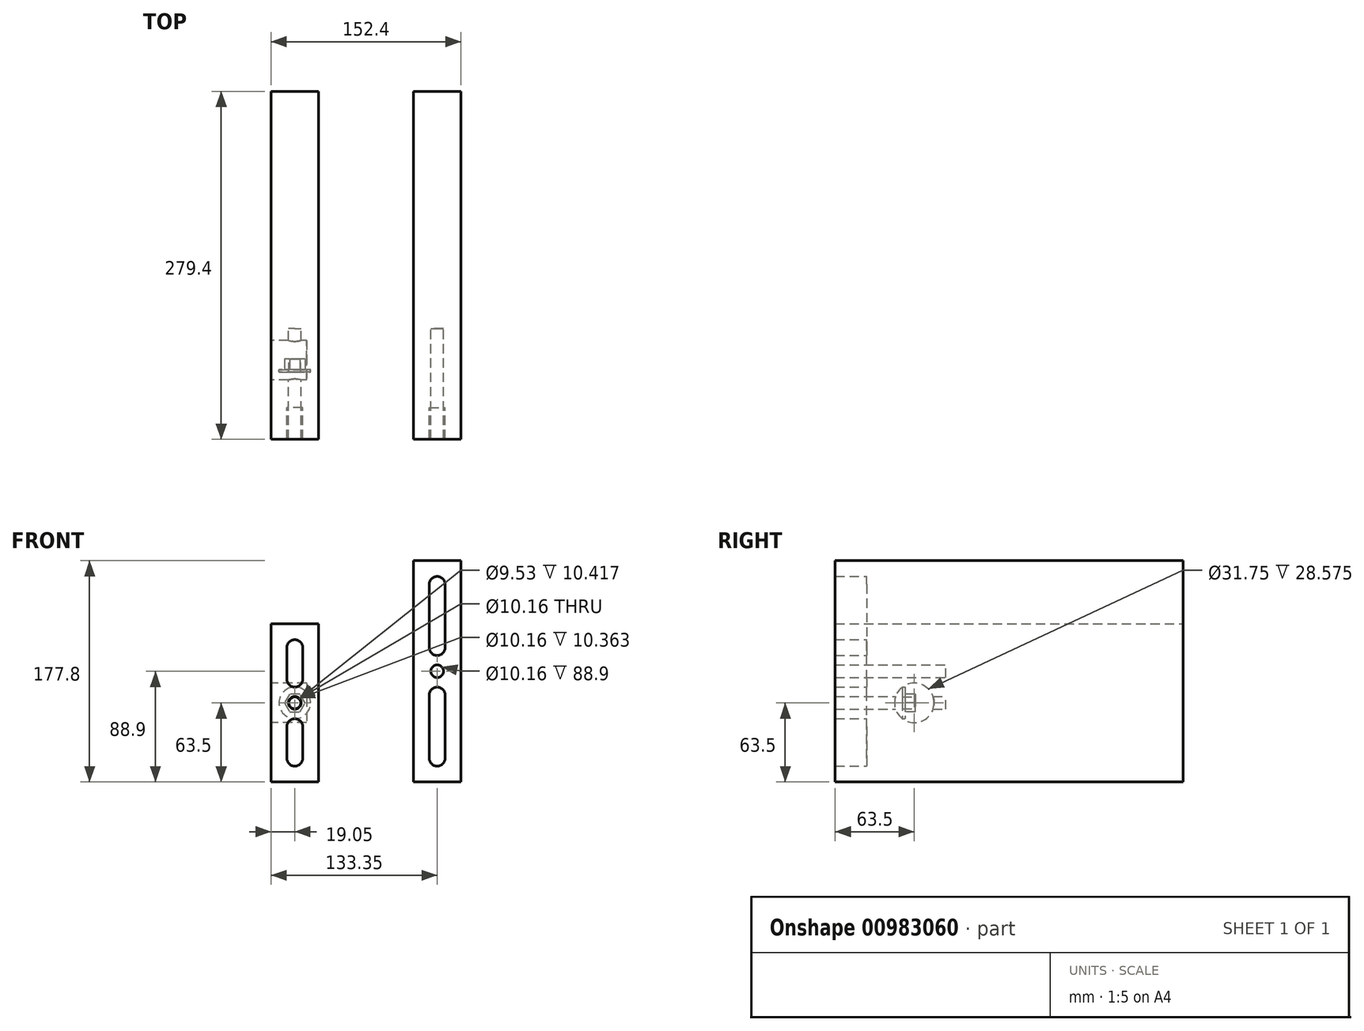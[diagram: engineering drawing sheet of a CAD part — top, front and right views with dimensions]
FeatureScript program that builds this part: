
annotation { "Feature Type Name" : "Feature", "Feature Type Description" : "" }
export const myFeature = defineFeature(function(context is Context, id is Id, definition is map)
    precondition{}
    {
        {
            var Q0;
            Q0=qCreatedBy(makeId("Front.planeOp"),FACE);
            var sketch = newSketch(context, id + "F0", { "sketchPlane" : qUnion([Q0])});
            skLineSegment(sketch, "E0.bottom", {"start": v(0, 0) * mm, "end": v(-38.1, 0) * mm});
            skLineSegment(sketch, "E0.top", {"start": v(0, 127) * mm, "end": v(-38.1, 127) * mm});
            skLineSegment(sketch, "E0.left", {"start": v(0, 0) * mm, "end": v(0, 127) * mm});
            skLineSegment(sketch, "E0.right", {"start": v(-38.1, 0) * mm, "end": v(-38.1, 127) * mm});
            skLineSegment(sketch, "E1.bottom", {"start": v(76.2, 0) * mm, "end": v(114.3, 0) * mm});
            skLineSegment(sketch, "E1.top", {"start": v(76.2, 177.8) * mm, "end": v(114.3, 177.8) * mm});
            skLineSegment(sketch, "E1.left", {"start": v(76.2, 0) * mm, "end": v(76.2, 177.8) * mm});
            skLineSegment(sketch, "E1.right", {"start": v(114.3, 0) * mm, "end": v(114.3, 177.8) * mm});
            skLineSegment(sketch, "E2", {"start": v(-19.05, 44.45) * mm, "end": v(-19.05, 19.05) * mm, "construction": true});
            skArc(sketch, "E3.0.startCap", {"start": v(-25.4, 44.45) * mm, "mid": v(-19.05, 50.8) * mm, "end": v(-12.7, 44.45) * mm});
            skArc(sketch, "E3.0.endCap", {"start": v(-12.7, 19.05) * mm, "mid": v(-19.05, 12.7) * mm, "end": v(-25.4, 19.05) * mm});
            skLineSegment(sketch, "E3.0.left", {"start": v(-12.7, 44.45) * mm, "end": v(-12.7, 19.05) * mm});
            skLineSegment(sketch, "E3.0.right", {"start": v(-25.4, 44.45) * mm, "end": v(-25.4, 19.05) * mm});
            skLineSegment(sketch, "E4", {"start": v(-38.1, 63.5) * mm, "end": v(0, 63.5) * mm, "construction": true});
            skArc(sketch, "E5.MirrorCS", {"start": v(-12.7, 44.45) * mm, "mid": v(-19.05, 50.8) * mm, "end": v(-25.4, 44.45) * mm});
            skArc(sketch, "E6.MirrorCS", {"start": v(-25.4, 19.05) * mm, "mid": v(-19.05, 12.7) * mm, "end": v(-12.7, 19.05) * mm});
            skLineSegment(sketch, "E7.MirrorCS", {"start": v(0, 63.5) * mm, "end": v(-38.1, 63.5) * mm, "construction": true});
            skArc(sketch, "E8.MirrorCS", {"start": v(-12.7, 82.55) * mm, "mid": v(-19.05, 76.2) * mm, "end": v(-25.4, 82.55) * mm});
            skLineSegment(sketch, "E9.MirrorCS", {"start": v(-25.4, 82.55) * mm, "end": v(-25.4, 107.95) * mm});
            skLineSegment(sketch, "E10.MirrorCS", {"start": v(-12.7, 82.55) * mm, "end": v(-12.7, 107.95) * mm});
            skArc(sketch, "E11.MirrorCS", {"start": v(-12.7, 107.95) * mm, "mid": v(-19.05, 114.3) * mm, "end": v(-25.4, 107.95) * mm});
            skLineSegment(sketch, "E12", {"start": v(-19.05, 19.05) * mm, "end": v(-19.05, 0) * mm, "construction": true});
            skCircle(sketch, "E13", {"center": v(-19.05, 63.5) * mm, "radius": 5.08 * mm});
            skLineSegment(sketch, "E14", {"start": v(95.25, 19.05) * mm, "end": v(95.25, 69.85) * mm, "construction": true});
            skLineSegment(sketch, "E15", {"start": v(95.25, 19.05) * mm, "end": v(95.25, 0) * mm, "construction": true});
            skArc(sketch, "E16.0.startCap", {"start": v(101.6, 19.05) * mm, "mid": v(95.25, 12.7) * mm, "end": v(88.9, 19.05) * mm});
            skArc(sketch, "E16.0.endCap", {"start": v(88.9, 69.85) * mm, "mid": v(95.25, 76.2) * mm, "end": v(101.6, 69.85) * mm});
            skLineSegment(sketch, "E16.0.left", {"start": v(88.9, 19.05) * mm, "end": v(88.9, 69.85) * mm});
            skLineSegment(sketch, "E16.0.right", {"start": v(101.6, 19.05) * mm, "end": v(101.6, 69.85) * mm});
            skLineSegment(sketch, "E17", {"start": v(76.2, 88.9) * mm, "end": v(114.3, 88.9) * mm, "construction": true});
            skArc(sketch, "E18.MirrorCS", {"start": v(88.9, 107.95) * mm, "mid": v(95.25, 101.6) * mm, "end": v(101.6, 107.95) * mm});
            skLineSegment(sketch, "E19.MirrorCS", {"start": v(88.9, 158.75) * mm, "end": v(88.9, 107.95) * mm});
            skLineSegment(sketch, "E20.MirrorCS", {"start": v(101.6, 158.75) * mm, "end": v(101.6, 107.95) * mm});
            skArc(sketch, "E21.MirrorCS", {"start": v(101.6, 158.75) * mm, "mid": v(95.25, 165.1) * mm, "end": v(88.9, 158.75) * mm});
            skCircle(sketch, "E22", {"center": v(95.25, 88.9) * mm, "radius": 5.08 * mm});
            skSolve(sketch);
        }
        {
            var Q0;
            Q0 = qSketchRegion(id + "F0", true);
            extrude(context, id + "F1", {"entities" : qUnion([Q0]), "depth" : 25.4 * mm, "offsetDistance" : 25.4 * mm});
        }
        {
            var Q0;
            Q0=makeQuery(id+"F1.opExtrude","CAP_FACE",FACE,{"disambiguationData":[OSD([sQuery(id+"F0.wireOp",EDGE,"E1.bottom"),sQuery(id+"F0.wireOp",EDGE,"E1.top"),sQuery(id+"F0.wireOp",EDGE,"E1.left"),sQuery(id+"F0.wireOp",EDGE,"E1.right"),sQuery(id+"F0.wireOp",EDGE,"E16.0.startCap"),sQuery(id+"F0.wireOp",EDGE,"E16.0.endCap"),sQuery(id+"F0.wireOp",EDGE,"E16.0.left"),sQuery(id+"F0.wireOp",EDGE,"E16.0.right"),sQuery(id+"F0.wireOp",EDGE,"E18.MirrorCS"),sQuery(id+"F0.wireOp",EDGE,"E19.MirrorCS"),sQuery(id+"F0.wireOp",EDGE,"E20.MirrorCS"),sQuery(id+"F0.wireOp",EDGE,"E21.MirrorCS"),sQuery(id+"F0.wireOp",EDGE,"E22")])],"isStart":true});
            var sketch = newSketch(context, id + "F2", { "sketchPlane" : qUnion([Q0])});
            skLineSegment(sketch, "E23.bottom", {"start": v(-114.3, 177.8) * mm, "end": v(-76.2, 177.8) * mm});
            skLineSegment(sketch, "E23.top", {"start": v(-114.3, 0) * mm, "end": v(-76.2, 0) * mm});
            skLineSegment(sketch, "E23.left", {"start": v(-114.3, 177.8) * mm, "end": v(-114.3, 0) * mm});
            skLineSegment(sketch, "E23.right", {"start": v(-76.2, 177.8) * mm, "end": v(-76.2, 0) * mm});
            skLineSegment(sketch, "E24.bottom", {"start": v(0, 0) * mm, "end": v(38.1, 0) * mm});
            skLineSegment(sketch, "E24.top", {"start": v(0, 127) * mm, "end": v(38.1, 127) * mm});
            skLineSegment(sketch, "E24.left", {"start": v(0, 0) * mm, "end": v(0, 127) * mm});
            skLineSegment(sketch, "E24.right", {"start": v(38.1, 0) * mm, "end": v(38.1, 127) * mm});
            skSolve(sketch);
        }
        {
            var Q0;
            Q0 = qSketchRegion(id + "F2", true);
            extrude(context, id + "F3", {"entities" : qUnion([Q0]), "operationType" : NewBodyOperationType.ADD, "depth" : 254 * mm, "offsetDistance" : 25.4 * mm});
        }
        {
            var Q0;
            Q0=makeQuery(id+"F3.boolean.opBoolean","SPLIT",FACE,{"disambiguationData":[TD([makeQuery(id+"F1.opExtrude","SWEPT_FACE",FACE,{"disambiguationData":[OSD([sQuery(id+"F0.wireOp",EDGE,"E8.MirrorCS")])]})])],"derivedFrom":makeQuery(id+"F3.opExtrude","CAP_FACE",FACE,{"disambiguationData":[OSD([sQuery(id+"F2.wireOp",EDGE,"E24.bottom"),sQuery(id+"F2.wireOp",EDGE,"E24.top"),sQuery(id+"F2.wireOp",EDGE,"E24.left"),sQuery(id+"F2.wireOp",EDGE,"E24.right")])],"isStart":true})});
            var sketch = newSketch(context, id + "F4", { "sketchPlane" : qUnion([Q0])});
            skCircle(sketch, "E25.0", {"center": v(-19.05, 63.5) * mm, "radius": 5.08 * mm});
            skCircle(sketch, "E26.0", {"center": v(95.25, 88.9) * mm, "radius": 5.08 * mm});
            skSolve(sketch);
        }
        {
            var Q0;
            Q0 = qSketchRegion(id + "F4", true);
            extrude(context, id + "F5", {"entities" : qUnion([Q0]), "operationType" : NewBodyOperationType.REMOVE, "oppositeDirection" : true, "depth" : 63.5 * mm, "offsetDistance" : 25.4 * mm});
        }
        {
            var Q0;
            Q0=makeQuery(id+"F3.boolean.opBoolean","MERGE",FACE,{"derivedFrom":[makeQuery(id+"F1.opExtrude","SWEPT_FACE",FACE,{"disambiguationData":[OSD([sQuery(id+"F0.wireOp",EDGE,"E0.right")])]}),makeQuery(id+"F3.opExtrude","SWEPT_FACE",FACE,{"disambiguationData":[OSD([sQuery(id+"F2.wireOp",EDGE,"E24.right")])]})]});
            var sketch = newSketch(context, id + "F6", { "sketchPlane" : qUnion([Q0])});
            skCircle(sketch, "E27", {"center": v(-38.1, 63.5) * mm, "radius": 15.88 * mm});
            skSolve(sketch);
        }
        {
            var Q0;
            Q0 = qSketchRegion(id + "F6", true);
            extrude(context, id + "F7", {"entities" : qUnion([Q0]), "operationType" : NewBodyOperationType.REMOVE, "oppositeDirection" : true, "depth" : 28.57 * mm, "offsetDistance" : 25.4 * mm});
        }
        {
            var Q0;
            Q0=makeQuery(id+"F1.opExtrude","CAP_EDGE",EDGE,{"disambiguationData":[OSD([sQuery(id+"F0.wireOp",EDGE,"E0.top")])],"isStart":false});
            cPoint(context, id + "F8", {"entities" : qUnion([Q0]), "parameter" : 0.5});
        }
        {
            var Q0;
            Q0 = qCreatedBy(id + "F8" ,VERTEX);
            var Q1;
            Q1=makeQuery(id+"F3.boolean.opBoolean","MERGE",FACE,{"derivedFrom":[makeQuery(id+"F1.opExtrude","SWEPT_FACE",FACE,{"disambiguationData":[OSD([sQuery(id+"F0.wireOp",EDGE,"E0.right")])]}),makeQuery(id+"F3.opExtrude","SWEPT_FACE",FACE,{"disambiguationData":[OSD([sQuery(id+"F2.wireOp",EDGE,"E24.right")])]})]});
            cPlane(context, id + "F9", {"entities" : qUnion([Q0, Q1]), "cplaneType" : CPlaneType.PLANE_POINT, "offset" : 25.4 * mm, "width" : 152.4 * mm, "height" : 152.4 * mm});
        }
        {
            var Q0;
            Q0=qCreatedBy(id+"F9.planeOp",FACE);
            var sketch = newSketch(context, id + "F10", { "sketchPlane" : qUnion([Q0])});
            skLineSegment(sketch, "E28.bottom", {"start": v(-30.66, 76.2) * mm, "end": v(-28.58, 76.2) * mm});
            skLineSegment(sketch, "E28.top", {"start": v(-30.66, 68.26) * mm, "end": v(-28.58, 68.26) * mm});
            skLineSegment(sketch, "E28.left", {"start": v(-30.66, 76.2) * mm, "end": v(-30.66, 68.26) * mm});
            skLineSegment(sketch, "E28.right", {"start": v(-28.58, 76.2) * mm, "end": v(-28.58, 68.26) * mm});
            skLineSegment(sketch, "E29", {"start": v(-44.6, 63.5) * mm, "end": v(25.4, 63.5) * mm, "construction": true});
            skSolve(sketch);
        }
        {
            var Q0;
            Q0=makeQuery(id+"F10.imprint","IMPRINT",FACE,{"disambiguationData":[TD([[makeQuery(id+"F10.imprint","IMPRINT",EDGE,{"derivedFrom":sQuery(id+"F10.wireOp",EDGE,"E28.bottom")}),-1.0]])]});
            var Q1;
            Q1=sQuery(id+"F10.wireOp",EDGE,"E29");
            revolve(context, id + "F11", {"surfaceOperationType" : NewSurfaceOperationType.NEW, "entities" : qUnion([Q0]), "axis" : qUnion([Q1]), "revolveType" : RevolveType.FULL});
        }
        {
            var Q0;
            Q0=makeQuery(id+"F11.opRevolve","SWEPT_FACE",FACE,{"disambiguationData":[OSD([sQuery(id+"F10.wireOp",EDGE,"E28.left")])]});
            var sketch = newSketch(context, id + "F12", { "sketchPlane" : qUnion([Q0])});
            skCircle(sketch, "E30.cCircle", {"center": v(19.05, 63.5) * mm, "radius": 7.14 * mm, "construction": true});
            skLineSegment(sketch, "E30.0", {"start": v(23.17, 70.64) * mm, "end": v(27.3, 63.5) * mm});
            skLineSegment(sketch, "E30.1", {"start": v(27.3, 63.5) * mm, "end": v(23.17, 56.36) * mm});
            skLineSegment(sketch, "E30.2", {"start": v(23.17, 56.36) * mm, "end": v(14.93, 56.36) * mm});
            skLineSegment(sketch, "E30.3", {"start": v(14.93, 56.36) * mm, "end": v(10.8, 63.5) * mm});
            skLineSegment(sketch, "E30.4", {"start": v(10.8, 63.5) * mm, "end": v(14.93, 70.64) * mm});
            skLineSegment(sketch, "E30.5", {"start": v(14.93, 70.64) * mm, "end": v(23.17, 70.64) * mm});
            skPoint(sketch, "E30.0.midPoint", {"position": v(25.24, 67.07) * mm});
            skCircle(sketch, "E31.0", {"center": v(19.05, 63.5) * mm, "radius": 4.76 * mm});
            skSolve(sketch);
        }
        {
            var Q0;
            Q0 = qSketchRegion(id + "F12", true);
            extrude(context, id + "F13", {"entities" : qUnion([Q0]), "operationType" : NewBodyOperationType.ADD, "depth" : 8.33 * mm, "offsetDistance" : 25.4 * mm});
        }
    });
